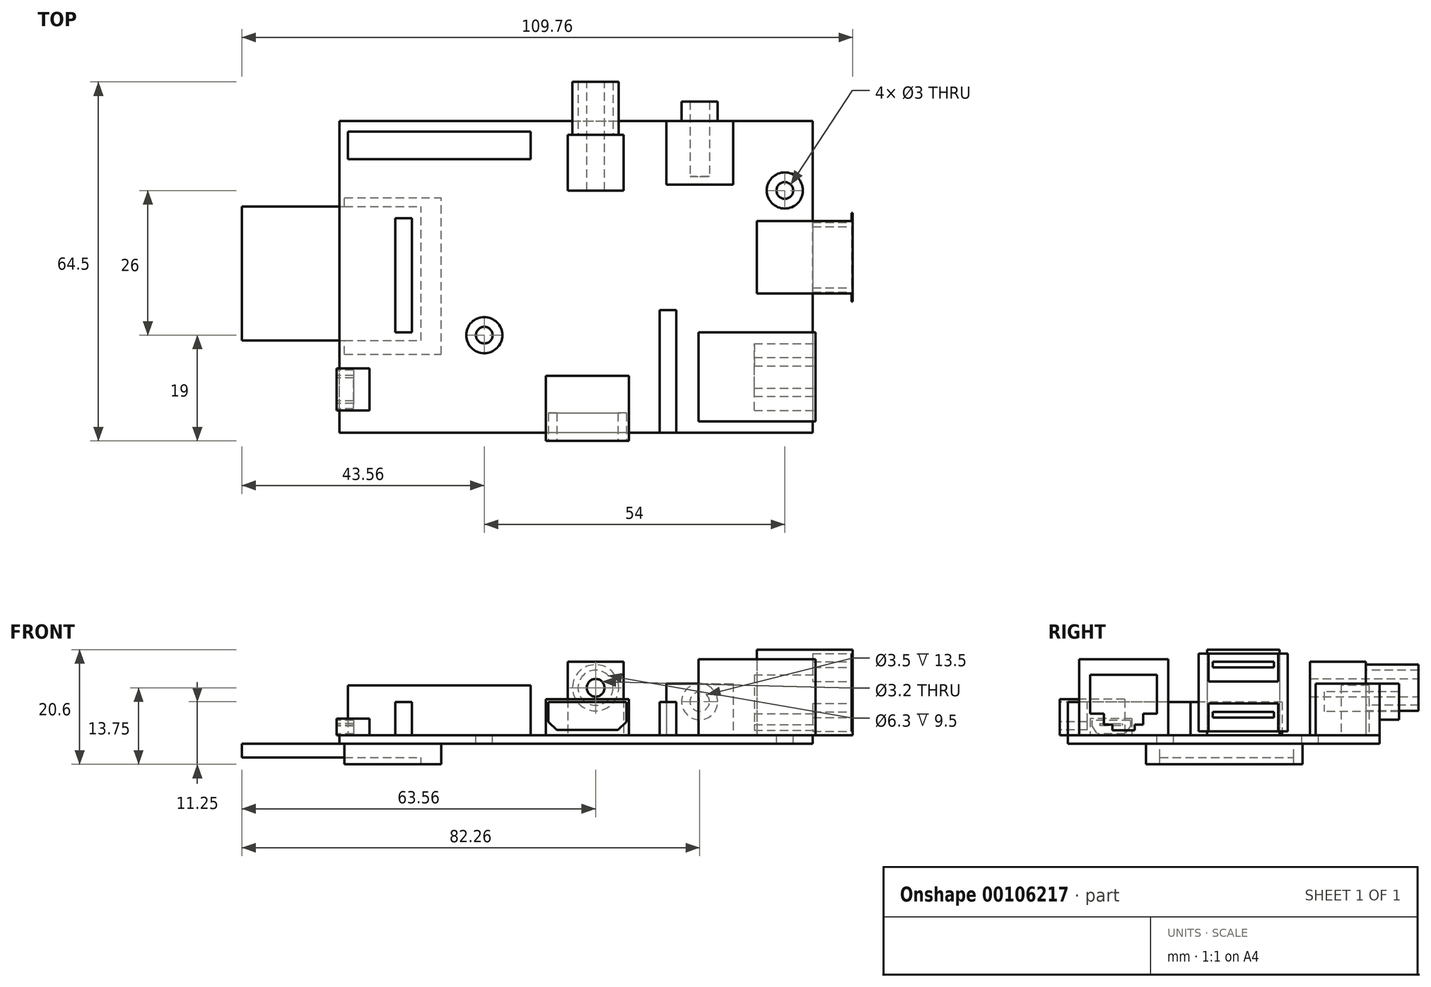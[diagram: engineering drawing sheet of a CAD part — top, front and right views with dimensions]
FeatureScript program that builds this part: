
annotation { "Feature Type Name" : "Feature", "Feature Type Description" : "" }
export const myFeature = defineFeature(function(context is Context, id is Id, definition is map)
    precondition{}
    {
        {
            var Q0;
            Q0=qCreatedBy(makeId("Top.planeOp"),FACE);
            var sketch = newSketch(context, id + "F0", { "sketchPlane" : qUnion([Q0])});
            skLineSegment(sketch, "E0", {"start": v(-47.7, 28) * mm, "end": v(37.3, 28) * mm});
            skLineSegment(sketch, "E1", {"start": v(37.3, 28) * mm, "end": v(37.3, -28) * mm});
            skLineSegment(sketch, "E2", {"start": v(37.3, -28) * mm, "end": v(-47.7, -28) * mm});
            skLineSegment(sketch, "E3", {"start": v(-47.7, -28) * mm, "end": v(-47.7, 28) * mm});
            skCircle(sketch, "E4", {"center": v(32.3, 15.5) * mm, "radius": 3.25 * mm});
            skCircle(sketch, "E5", {"center": v(-21.7, -10.5) * mm, "radius": 3.25 * mm});
            skLineSegment(sketch, "E6.bottom", {"start": v(37.8, -10) * mm, "end": v(16.8, -10) * mm});
            skLineSegment(sketch, "E6.top", {"start": v(37.8, -26) * mm, "end": v(16.8, -26) * mm});
            skLineSegment(sketch, "E6.left", {"start": v(37.8, -10) * mm, "end": v(37.8, -26) * mm});
            skLineSegment(sketch, "E6.right", {"start": v(16.8, -10) * mm, "end": v(16.8, -26) * mm});
            skLineSegment(sketch, "E7.bottom", {"start": v(27.3, 10) * mm, "end": v(44.3, 10) * mm});
            skLineSegment(sketch, "E7.top", {"start": v(27.3, -3) * mm, "end": v(44.3, -3) * mm});
            skLineSegment(sketch, "E7.left", {"start": v(27.3, 10) * mm, "end": v(27.3, -3) * mm});
            skLineSegment(sketch, "E7.right", {"start": v(44.3, 10) * mm, "end": v(44.3, -3) * mm});
            skLineSegment(sketch, "E8", {"start": v(0, 28) * mm, "end": v(0, -28) * mm, "construction": true});
            skLineSegment(sketch, "E9", {"start": v(-47.7, 0) * mm, "end": v(37.3, 0) * mm, "construction": true});
            skPoint(sketch, "E10", {"position": v(0, 0) * mm});
            skLineSegment(sketch, "E11.bottom", {"start": v(-10.64, -17.8) * mm, "end": v(4.3, -17.8) * mm});
            skLineSegment(sketch, "E11.top", {"start": v(-10.64, -29.5) * mm, "end": v(4.3, -29.5) * mm});
            skLineSegment(sketch, "E11.left", {"start": v(-10.64, -17.8) * mm, "end": v(-10.64, -29.5) * mm});
            skLineSegment(sketch, "E11.right", {"start": v(4.3, -17.8) * mm, "end": v(4.3, -29.5) * mm});
            skLineSegment(sketch, "E12.bottom", {"start": v(11, 28.03) * mm, "end": v(23, 28.03) * mm});
            skLineSegment(sketch, "E12.top", {"start": v(11, 16.53) * mm, "end": v(23, 16.53) * mm});
            skLineSegment(sketch, "E12.left", {"start": v(11, 28.03) * mm, "end": v(11, 16.53) * mm});
            skLineSegment(sketch, "E12.right", {"start": v(23, 28.03) * mm, "end": v(23, 16.53) * mm});
            skLineSegment(sketch, "E13.bottom", {"start": v(-6.7, 25.5) * mm, "end": v(3.3, 25.5) * mm});
            skLineSegment(sketch, "E13.top", {"start": v(-6.7, 15.5) * mm, "end": v(3.3, 15.5) * mm});
            skLineSegment(sketch, "E13.left", {"start": v(-6.7, 25.5) * mm, "end": v(-6.7, 15.5) * mm});
            skLineSegment(sketch, "E13.right", {"start": v(3.3, 25.5) * mm, "end": v(3.3, 15.5) * mm});
            skLineSegment(sketch, "E14.bottom", {"start": v(-46.2, 26.1) * mm, "end": v(-13.4, 26.1) * mm});
            skLineSegment(sketch, "E14.top", {"start": v(-46.2, 21.1) * mm, "end": v(-13.4, 21.1) * mm});
            skLineSegment(sketch, "E14.left", {"start": v(-46.2, 26.1) * mm, "end": v(-46.2, 21.1) * mm});
            skLineSegment(sketch, "E14.right", {"start": v(-13.4, 26.1) * mm, "end": v(-13.4, 21.1) * mm});
            skLineSegment(sketch, "E15.bottom", {"start": v(-46.7, 14.11) * mm, "end": v(-29.7, 14.11) * mm});
            skLineSegment(sketch, "E15.top", {"start": v(-46.7, -13.89) * mm, "end": v(-29.7, -13.89) * mm});
            skLineSegment(sketch, "E15.left", {"start": v(-46.7, 14.11) * mm, "end": v(-46.7, -13.89) * mm});
            skLineSegment(sketch, "E15.right", {"start": v(-29.7, 14.11) * mm, "end": v(-29.7, -13.89) * mm});
            skLineSegment(sketch, "E16.bottom", {"start": v(-65.2, 12.61) * mm, "end": v(-33.2, 12.61) * mm});
            skLineSegment(sketch, "E16.top", {"start": v(-65.2, -11.39) * mm, "end": v(-33.2, -11.39) * mm});
            skLineSegment(sketch, "E16.left", {"start": v(-65.2, 12.61) * mm, "end": v(-65.2, -11.39) * mm});
            skLineSegment(sketch, "E16.right", {"start": v(-33.2, 12.61) * mm, "end": v(-33.2, -11.39) * mm});
            skLineSegment(sketch, "E17.bottom", {"start": v(-48.2, -16.5) * mm, "end": v(-42.3, -16.5) * mm});
            skLineSegment(sketch, "E17.top", {"start": v(-48.2, -24) * mm, "end": v(-42.3, -24) * mm});
            skLineSegment(sketch, "E17.left", {"start": v(-48.2, -16.5) * mm, "end": v(-48.2, -24) * mm});
            skLineSegment(sketch, "E17.right", {"start": v(-42.3, -16.5) * mm, "end": v(-42.3, -24) * mm});
            skLineSegment(sketch, "E18.bottom", {"start": v(9.8, -6) * mm, "end": v(12.8, -6) * mm});
            skLineSegment(sketch, "E18.top", {"start": v(9.8, -28) * mm, "end": v(12.8, -28) * mm});
            skLineSegment(sketch, "E18.left", {"start": v(9.8, -6) * mm, "end": v(9.8, -28) * mm});
            skLineSegment(sketch, "E18.right", {"start": v(12.8, -6) * mm, "end": v(12.8, -28) * mm});
            skCircle(sketch, "E19", {"center": v(32.3, 15.5) * mm, "radius": 1.5 * mm});
            skCircle(sketch, "E20", {"center": v(-21.7, -10.5) * mm, "radius": 1.5 * mm});
            skLineSegment(sketch, "E21.bottom", {"start": v(-37.7, 10.5) * mm, "end": v(-34.7, 10.5) * mm});
            skLineSegment(sketch, "E21.top", {"start": v(-37.7, -10) * mm, "end": v(-34.7, -10) * mm});
            skLineSegment(sketch, "E21.left", {"start": v(-37.7, 10.5) * mm, "end": v(-37.7, -10) * mm});
            skLineSegment(sketch, "E21.right", {"start": v(-34.7, 10.5) * mm, "end": v(-34.7, -10) * mm});
            skSolve(sketch);
        }
        {
            var Q0;
            {var subQ9=sQuery(id+"F0.wireOp",EDGE,"E0");Q0=makeQuery(id+"F0.imprint","IMPRINT",FACE,{"disambiguationData":[TD([[makeQuery(id+"F0.imprint","IMPRINT",EDGE,{"derivedFrom":subQ9}),-1.0]])]});}
            var Q1;
            {var subQ5=sQuery(id+"F0.wireOp",EDGE,"E7.left");Q1=makeQuery(id+"F0.imprint","IMPRINT",FACE,{"disambiguationData":[TD([[makeQuery(id+"F0.imprint","IMPRINT",EDGE,{"derivedFrom":subQ5}),1.0]])]});}
            var Q2;
            Q2=makeQuery(id+"F0.imprint","IMPRINT",FACE,{"disambiguationData":[TD([[makeQuery(id+"F0.imprint","IMPRINT",EDGE,{"derivedFrom":sQuery(id+"F0.wireOp",EDGE,"E4")}),1.0]])]});
            var Q3;
            Q3=makeQuery(id+"F0.imprint","IMPRINT",FACE,{"disambiguationData":[TD([[makeQuery(id+"F0.imprint","IMPRINT",EDGE,{"derivedFrom":sQuery(id+"F0.wireOp",EDGE,"E5")}),1.0]])]});
            var Q4;
            {var subQ5=sQuery(id+"F0.wireOp",EDGE,"E6.right");Q4=makeQuery(id+"F0.imprint","IMPRINT",FACE,{"disambiguationData":[TD([[makeQuery(id+"F0.imprint","IMPRINT",EDGE,{"derivedFrom":subQ5}),1.0]])]});}
            var Q5;
            {var subQ5=sQuery(id+"F0.wireOp",EDGE,"E15.bottom");Q5=makeQuery(id+"F0.imprint","IMPRINT",FACE,{"disambiguationData":[TD([[makeQuery(id+"F0.imprint","IMPRINT",EDGE,{"derivedFrom":subQ5}),-1.0]])]});}
            var Q6;
            {var subQ5=sQuery(id+"F0.wireOp",EDGE,"E16.right");Q6=makeQuery(id+"F0.imprint","IMPRINT",FACE,{"disambiguationData":[TD([[makeQuery(id+"F0.imprint","IMPRINT",EDGE,{"derivedFrom":subQ5}),-1.0]])]});}
            var Q7;
            {var subQ0=sQuery(id+"F0.wireOp",EDGE,"E16.top");var subQ1=sQuery(id+"F0.wireOp",EDGE,"E3");var subQ2=makeQuery(id+"F0.imprint","INTERSECT",VERTEX,{"derivedFrom":[subQ1,subQ0]});Q7=makeQuery(id+"F0.imprint","IMPRINT",FACE,{"disambiguationData":[TD([[makeQuery(id+"F0.imprint","IMPRINT",EDGE,{"disambiguationData":[TD([[subQ2,-1.0]])],"derivedFrom":subQ1}),-1.0]])]});}
            var Q8;
            {var subQ5=sQuery(id+"F0.wireOp",EDGE,"E17.right");Q8=makeQuery(id+"F0.imprint","IMPRINT",FACE,{"disambiguationData":[TD([[makeQuery(id+"F0.imprint","IMPRINT",EDGE,{"derivedFrom":subQ5}),-1.0]])]});}
            var Q9;
            Q9=makeQuery(id+"F0.imprint","IMPRINT",FACE,{"disambiguationData":[TD([[makeQuery(id+"F0.imprint","IMPRINT",EDGE,{"derivedFrom":sQuery(id+"F0.wireOp",EDGE,"E14.bottom")}),-1.0]])]});
            var Q10;
            Q10=makeQuery(id+"F0.imprint","IMPRINT",FACE,{"disambiguationData":[TD([[makeQuery(id+"F0.imprint","IMPRINT",EDGE,{"derivedFrom":sQuery(id+"F0.wireOp",EDGE,"E13.bottom")}),-1.0]])]});
            var Q11;
            {var subQ5=sQuery(id+"F0.wireOp",EDGE,"E12.top");Q11=makeQuery(id+"F0.imprint","IMPRINT",FACE,{"disambiguationData":[TD([[makeQuery(id+"F0.imprint","IMPRINT",EDGE,{"derivedFrom":subQ5}),1.0]])]});}
            var Q12;
            {var subQ5=sQuery(id+"F0.wireOp",EDGE,"E11.bottom");Q12=makeQuery(id+"F0.imprint","IMPRINT",FACE,{"disambiguationData":[TD([[makeQuery(id+"F0.imprint","IMPRINT",EDGE,{"derivedFrom":subQ5}),-1.0]])]});}
            var Q13;
            Q13=makeQuery(id+"F0.imprint","IMPRINT",FACE,{"disambiguationData":[TD([[makeQuery(id+"F0.imprint","IMPRINT",EDGE,{"derivedFrom":sQuery(id+"F0.wireOp",EDGE,"E18.bottom")}),-1.0]])]});
            var Q14;
            Q14=makeQuery(id+"F0.imprint","IMPRINT",FACE,{"disambiguationData":[TD([[makeQuery(id+"F0.imprint","IMPRINT",EDGE,{"derivedFrom":sQuery(id+"F0.wireOp",EDGE,"E21.bottom")}),-1.0]])]});
            extrude(context, id + "F1", {"entities" : qUnion([Q0, Q1, Q2, Q3, Q4, Q5, Q6, Q7, Q8, Q9, Q10, Q11, Q12, Q13, Q14]), "oppositeDirection" : true, "depth" : 1.5 * mm});
        }
        {
            var Q0;
            {var subQ5=sQuery(id+"F0.wireOp",EDGE,"E6.right");Q0=makeQuery(id+"F0.imprint","IMPRINT",FACE,{"disambiguationData":[TD([[makeQuery(id+"F0.imprint","IMPRINT",EDGE,{"derivedFrom":subQ5}),1.0]])]});}
            var Q1;
            {var subQ5=sQuery(id+"F0.wireOp",EDGE,"E6.left");Q1=makeQuery(id+"F0.imprint","IMPRINT",FACE,{"disambiguationData":[TD([[makeQuery(id+"F0.imprint","IMPRINT",EDGE,{"derivedFrom":subQ5}),-1.0]])]});}
            extrude(context, id + "F2", {"entities" : qUnion([Q0, Q1]), "depth" : 13.7 * mm});
        }
        {
            var Q0;
            {var subQ5=sQuery(id+"F0.wireOp",EDGE,"E7.left");Q0=makeQuery(id+"F0.imprint","IMPRINT",FACE,{"disambiguationData":[TD([[makeQuery(id+"F0.imprint","IMPRINT",EDGE,{"derivedFrom":subQ5}),1.0]])]});}
            var Q1;
            {var subQ5=sQuery(id+"F0.wireOp",EDGE,"E7.right");Q1=makeQuery(id+"F0.imprint","IMPRINT",FACE,{"disambiguationData":[TD([[makeQuery(id+"F0.imprint","IMPRINT",EDGE,{"derivedFrom":subQ5}),-1.0]])]});}
            extrude(context, id + "F3", {"entities" : qUnion([Q0, Q1]), "depth" : 15.4 * mm});
        }
        {
            var Q0;
            {var subQ5=sQuery(id+"F0.wireOp",EDGE,"E12.top");Q0=makeQuery(id+"F0.imprint","IMPRINT",FACE,{"disambiguationData":[TD([[makeQuery(id+"F0.imprint","IMPRINT",EDGE,{"derivedFrom":subQ5}),1.0]])]});}
            extrude(context, id + "F4", {"entities" : qUnion([Q0]), "depth" : 9.3 * mm});
        }
        {
            var Q0;
            Q0=makeQuery(id+"F0.imprint","IMPRINT",FACE,{"disambiguationData":[TD([[makeQuery(id+"F0.imprint","IMPRINT",EDGE,{"derivedFrom":sQuery(id+"F0.wireOp",EDGE,"E13.bottom")}),-1.0]])]});
            extrude(context, id + "F5", {"entities" : qUnion([Q0]), "depth" : 13.2 * mm});
        }
        {
            var Q0;
            Q0=makeQuery(id+"F0.imprint","IMPRINT",FACE,{"disambiguationData":[TD([[makeQuery(id+"F0.imprint","IMPRINT",EDGE,{"derivedFrom":sQuery(id+"F0.wireOp",EDGE,"E14.bottom")}),-1.0]])]});
            extrude(context, id + "F6", {"entities" : qUnion([Q0]), "depth" : 9 * mm});
        }
        {
            var Q0;
            Q0=makeQuery(id+"F0.imprint","IMPRINT",FACE,{"disambiguationData":[TD([[makeQuery(id+"F0.imprint","IMPRINT",EDGE,{"derivedFrom":sQuery(id+"F0.wireOp",EDGE,"E18.bottom")}),-1.0]])]});
            extrude(context, id + "F7", {"entities" : qUnion([Q0]), "depth" : 6 * mm});
        }
        {
            var Q0;
            {var subQ5=sQuery(id+"F0.wireOp",EDGE,"E11.bottom");Q0=makeQuery(id+"F0.imprint","IMPRINT",FACE,{"disambiguationData":[TD([[makeQuery(id+"F0.imprint","IMPRINT",EDGE,{"derivedFrom":subQ5}),-1.0]])]});}
            var Q1;
            {var subQ5=sQuery(id+"F0.wireOp",EDGE,"E11.top");Q1=makeQuery(id+"F0.imprint","IMPRINT",FACE,{"disambiguationData":[TD([[makeQuery(id+"F0.imprint","IMPRINT",EDGE,{"derivedFrom":subQ5}),1.0]])]});}
            extrude(context, id + "F8", {"entities" : qUnion([Q0, Q1]), "depth" : 6.5 * mm});
        }
        {
            var Q0;
            Q0=makeQuery(id+"F0.imprint","IMPRINT",FACE,{"disambiguationData":[TD([[makeQuery(id+"F0.imprint","IMPRINT",EDGE,{"derivedFrom":sQuery(id+"F0.wireOp",EDGE,"E4")}),1.0]])]});
            var Q1;
            Q1=makeQuery(id+"F0.imprint","IMPRINT",FACE,{"disambiguationData":[TD([[makeQuery(id+"F0.imprint","IMPRINT",EDGE,{"derivedFrom":sQuery(id+"F0.wireOp",EDGE,"E5")}),1.0]])]});
            extrude(context, id + "F9", {"entities" : qUnion([Q0, Q1]), "depth" : 0.01 * mm});
        }
        {
            var Q0;
            {var subQ5=sQuery(id+"F0.wireOp",EDGE,"E17.right");Q0=makeQuery(id+"F0.imprint","IMPRINT",FACE,{"disambiguationData":[TD([[makeQuery(id+"F0.imprint","IMPRINT",EDGE,{"derivedFrom":subQ5}),-1.0]])]});}
            var Q1;
            {var subQ5=sQuery(id+"F0.wireOp",EDGE,"E17.left");Q1=makeQuery(id+"F0.imprint","IMPRINT",FACE,{"disambiguationData":[TD([[makeQuery(id+"F0.imprint","IMPRINT",EDGE,{"derivedFrom":subQ5}),1.0]])]});}
            extrude(context, id + "F10", {"entities" : qUnion([Q0, Q1]), "depth" : 3 * mm});
        }
        {
            var Q0;
            Q0=makeQuery(id+"F0.imprint","IMPRINT",FACE,{"disambiguationData":[TD([[makeQuery(id+"F0.imprint","IMPRINT",EDGE,{"derivedFrom":sQuery(id+"F0.wireOp",EDGE,"E21.bottom")}),-1.0]])]});
            extrude(context, id + "F11", {"entities" : qUnion([Q0]), "depth" : 6 * mm});
        }
        {
            var Q0;
            Q0=makeQuery(id+"F1.opExtrude","CAP_FACE",FACE,{"disambiguationData":[OSD([sQuery(id+"F0.wireOp",EDGE,"E0"),sQuery(id+"F0.wireOp",EDGE,"E1"),sQuery(id+"F0.wireOp",EDGE,"E2"),sQuery(id+"F0.wireOp",EDGE,"E3"),sQuery(id+"F0.wireOp",EDGE,"E18.top"),sQuery(id+"F0.wireOp",EDGE,"E19"),sQuery(id+"F0.wireOp",EDGE,"E20")])],"isStart":false});
            var sketch = newSketch(context, id + "F12", { "sketchPlane" : qUnion([Q0])});
            skLineSegment(sketch, "E22.bottom", {"start": v(-65.26, 11.49) * mm, "end": v(-33.09, 11.49) * mm});
            skLineSegment(sketch, "E22.top", {"start": v(-65.26, -12.6) * mm, "end": v(-33.09, -12.6) * mm});
            skLineSegment(sketch, "E22.left", {"start": v(-65.26, 11.49) * mm, "end": v(-65.26, -12.6) * mm});
            skLineSegment(sketch, "E22.right", {"start": v(-33.09, 11.49) * mm, "end": v(-33.09, -12.6) * mm});
            skLineSegment(sketch, "E23.bottom", {"start": v(-46.8, 13.96) * mm, "end": v(-29.45, 13.96) * mm});
            skLineSegment(sketch, "E23.top", {"start": v(-46.8, -14.17) * mm, "end": v(-29.45, -14.17) * mm});
            skLineSegment(sketch, "E23.left", {"start": v(-46.8, 13.96) * mm, "end": v(-46.8, -14.17) * mm});
            skLineSegment(sketch, "E23.right", {"start": v(-29.45, 13.96) * mm, "end": v(-29.45, -14.17) * mm});
            skSolve(sketch);
        }
        {
            var Q0;
            {var subQ1=sQuery(id+"F12.wireOp",EDGE,"E22.right");Q0=makeQuery(id+"F12.imprint","IMPRINT",FACE,{"disambiguationData":[TD([[makeQuery(id+"F12.imprint","IMPRINT",EDGE,{"derivedFrom":subQ1}),1.0]])]});}
            extrude(context, id + "F13", {"entities" : qUnion([Q0]), "depth" : 3.7 * mm});
        }
        {
            var Q0;
            {var subQ0=sQuery(id+"F12.wireOp",EDGE,"E22.right");Q0=makeQuery(id+"F12.imprint","IMPRINT",FACE,{"disambiguationData":[TD([[makeQuery(id+"F12.imprint","IMPRINT",EDGE,{"derivedFrom":subQ0}),-1.0]])]});}
            var Q1;
            {var subQ0=sQuery(id+"F12.wireOp",EDGE,"E23.left");var subQ1=sQuery(id+"F12.wireOp",EDGE,"E22.bottom");var subQ2=makeQuery(id+"F12.imprint","INTERSECT",VERTEX,{"derivedFrom":[subQ1,subQ0]});Q1=makeQuery(id+"F12.imprint","IMPRINT",FACE,{"disambiguationData":[TD([[makeQuery(id+"F12.imprint","IMPRINT",EDGE,{"disambiguationData":[TD([[subQ2,1.0]])],"derivedFrom":subQ1}),-1.0]])]});}
            var Q2;
            {var subQ0=sQuery(id+"F12.wireOp",EDGE,"E22.left");Q2=makeQuery(id+"F12.imprint","IMPRINT",FACE,{"disambiguationData":[TD([[makeQuery(id+"F12.imprint","IMPRINT",EDGE,{"derivedFrom":subQ0}),1.0]])]});}
            extrude(context, id + "F14", {"entities" : qUnion([Q0, Q1, Q2]), "operationType" : NewBodyOperationType.ADD, "depth" : 2.5 * mm});
        }
        {
            var Q0;
            Q0=makeQuery(id+"F4.opExtrude","SWEPT_FACE",FACE,{"disambiguationData":[OSD([sQuery(id+"F0.wireOp",EDGE,"E0")])]});
            var sketch = newSketch(context, id + "F15", { "sketchPlane" : qUnion([Q0])});
            skLineSegment(sketch, "E24", {"start": v(-17, 9.3) * mm, "end": v(-17, 0) * mm, "construction": true});
            skCircle(sketch, "E25", {"center": v(-17, 6.05) * mm, "radius": 3.25 * mm});
            skCircle(sketch, "E26", {"center": v(-17, 6.05) * mm, "radius": 1.75 * mm});
            skSolve(sketch);
        }
        {
            var Q0;
            Q0=makeQuery(id+"F15.imprint","IMPRINT",FACE,{"disambiguationData":[TD([[makeQuery(id+"F15.imprint","IMPRINT",EDGE,{"derivedFrom":sQuery(id+"F15.wireOp",EDGE,"E25")}),1.0]])]});
            extrude(context, id + "F16", {"entities" : qUnion([Q0]), "operationType" : NewBodyOperationType.ADD, "depth" : 3.5 * mm});
        }
        {
            var Q0;
            Q0=makeQuery(id+"F15.imprint","IMPRINT",FACE,{"disambiguationData":[TD([[makeQuery(id+"F15.imprint","IMPRINT",EDGE,{"derivedFrom":sQuery(id+"F15.wireOp",EDGE,"E26")}),1.0]])]});
            var Q1;
            Q1=sQuery(id+"F15.wireOp",EDGE,"E26");
            extrude(context, id + "F17", {"entities" : qUnion([Q0]), "operationType" : NewBodyOperationType.REMOVE, "surfaceEntities" : qUnion([Q1]), "oppositeDirection" : true, "depth" : 10 * mm});
        }
        {
            var Q0;
            Q0=makeQuery(id+"F5.opExtrude","SWEPT_FACE",FACE,{"disambiguationData":[OSD([sQuery(id+"F0.wireOp",EDGE,"E13.bottom")])]});
            var sketch = newSketch(context, id + "F18", { "sketchPlane" : qUnion([Q0])});
            skLineSegment(sketch, "E27", {"start": v(1.7, 13.2) * mm, "end": v(1.7, 0) * mm, "construction": true});
            skLineSegment(sketch, "E28", {"start": v(-3.3, 12.7) * mm, "end": v(6.7, 12.7) * mm, "construction": true});
            skCircle(sketch, "E29", {"center": v(1.7, 8.55) * mm, "radius": 4.15 * mm});
            skCircle(sketch, "E30", {"center": v(1.7, 8.55) * mm, "radius": 3.15 * mm});
            skCircle(sketch, "E31", {"center": v(1.7, 8.55) * mm, "radius": 1.6 * mm});
            skSolve(sketch);
        }
        {
            var Q0;
            Q0=makeQuery(id+"F18.imprint","IMPRINT",FACE,{"disambiguationData":[TD([[makeQuery(id+"F18.imprint","IMPRINT",EDGE,{"derivedFrom":sQuery(id+"F18.wireOp",EDGE,"E31")}),1.0]])]});
            extrude(context, id + "F19", {"entities" : qUnion([Q0]), "operationType" : NewBodyOperationType.REMOVE, "endBound" : BoundingType.THROUGH_ALL, "oppositeDirection" : true, "depth" : 25 * mm});
        }
        {
            var Q0;
            Q0=makeQuery(id+"F18.imprint","IMPRINT",FACE,{"disambiguationData":[TD([[makeQuery(id+"F18.imprint","IMPRINT",EDGE,{"derivedFrom":sQuery(id+"F18.wireOp",EDGE,"E30")}),1.0]])]});
            extrude(context, id + "F20", {"entities" : qUnion([Q0]), "operationType" : NewBodyOperationType.ADD, "depth" : 9.5 * mm});
        }
        {
            var Q0;
            Q0=makeQuery(id+"F18.imprint","IMPRINT",FACE,{"disambiguationData":[TD([[makeQuery(id+"F18.imprint","IMPRINT",EDGE,{"derivedFrom":sQuery(id+"F18.wireOp",EDGE,"E29")}),1.0]])]});
            extrude(context, id + "F21", {"entities" : qUnion([Q0]), "depth" : 9.5 * mm});
        }
        {
            var Q0;
            Q0=makeQuery(id+"F8.opExtrude","SWEPT_FACE",FACE,{"disambiguationData":[OSD([sQuery(id+"F0.wireOp",EDGE,"E11.top")])]});
            var sketch = newSketch(context, id + "F22", { "sketchPlane" : qUnion([Q0])});
            skLineSegment(sketch, "E32", {"start": v(-10.64, 3.25) * mm, "end": v(4.3, 3.25) * mm, "construction": true});
            skLineSegment(sketch, "E33", {"start": v(-3.17, 6.5) * mm, "end": v(-3.17, 0) * mm, "construction": true});
            skLineSegment(sketch, "E34", {"start": v(3.83, 6) * mm, "end": v(3.83, 2.43) * mm});
            skLineSegment(sketch, "E35", {"start": v(3.83, 2.43) * mm, "end": v(2.33, 1) * mm});
            skLineSegment(sketch, "E36", {"start": v(-8.67, 1) * mm, "end": v(-10.17, 2.43) * mm});
            skLineSegment(sketch, "E37", {"start": v(-10.17, 2.43) * mm, "end": v(-10.17, 6) * mm});
            skLineSegment(sketch, "E38", {"start": v(-10.17, 6) * mm, "end": v(-3.17, 6) * mm});
            skLineSegment(sketch, "E39", {"start": v(-3.17, 6) * mm, "end": v(3.83, 6) * mm});
            skLineSegment(sketch, "E40", {"start": v(-8.67, 1) * mm, "end": v(-3.17, 1) * mm});
            skLineSegment(sketch, "E41", {"start": v(-3.17, 1) * mm, "end": v(2.33, 1) * mm});
            skSolve(sketch);
        }
        {
            var Q0;
            Q0=makeQuery(id+"F22.imprint","IMPRINT",FACE,{"disambiguationData":[TD([[makeQuery(id+"F22.imprint","IMPRINT",EDGE,{"derivedFrom":sQuery(id+"F22.wireOp",EDGE,"E34")}),-1.0]])]});
            extrude(context, id + "F23", {"entities" : qUnion([Q0]), "operationType" : NewBodyOperationType.REMOVE, "oppositeDirection" : true, "depth" : 5 * mm});
        }
        {
            var Q0;
            Q0=makeQuery(id+"F2.opExtrude","SWEPT_FACE",FACE,{"disambiguationData":[OSD([sQuery(id+"F0.wireOp",EDGE,"E6.left")])]});
            var sketch = newSketch(context, id + "F24", { "sketchPlane" : qUnion([Q0])});
            skLineSegment(sketch, "E42", {"start": v(-18, 13.7) * mm, "end": v(-18, 0) * mm, "construction": true});
            skLineSegment(sketch, "E43", {"start": v(-18, 10.9) * mm, "end": v(-12, 10.9) * mm});
            skLineSegment(sketch, "E44", {"start": v(-12, 10.9) * mm, "end": v(-12, 3.9) * mm});
            skLineSegment(sketch, "E45", {"start": v(-12, 3.9) * mm, "end": v(-14.5, 3.9) * mm});
            skLineSegment(sketch, "E46", {"start": v(-14.5, 3.9) * mm, "end": v(-14.5, 1.9) * mm});
            skLineSegment(sketch, "E47", {"start": v(-14.5, 1.9) * mm, "end": v(-16, 1.9) * mm});
            skLineSegment(sketch, "E48", {"start": v(-16, 1.9) * mm, "end": v(-16, 0.9) * mm});
            skLineSegment(sketch, "E49", {"start": v(-16, 0.9) * mm, "end": v(-18, 0.9) * mm});
            skLineSegment(sketch, "E50.MirrorCS", {"start": v(-18, 10.9) * mm, "end": v(-24, 10.9) * mm});
            skLineSegment(sketch, "E51.MirrorCS", {"start": v(-24, 10.9) * mm, "end": v(-24, 3.9) * mm});
            skLineSegment(sketch, "E52.MirrorCS", {"start": v(-24, 3.9) * mm, "end": v(-21.5, 3.9) * mm});
            skLineSegment(sketch, "E53.MirrorCS", {"start": v(-21.5, 3.9) * mm, "end": v(-21.5, 1.9) * mm});
            skLineSegment(sketch, "E54.MirrorCS", {"start": v(-21.5, 1.9) * mm, "end": v(-20, 1.9) * mm});
            skLineSegment(sketch, "E55.MirrorCS", {"start": v(-20, 1.9) * mm, "end": v(-20, 0.9) * mm});
            skLineSegment(sketch, "E56.MirrorCS", {"start": v(-20, 0.9) * mm, "end": v(-18, 0.9) * mm});
            skSolve(sketch);
        }
        {
            var Q0;
            Q0=makeQuery(id+"F24.imprint","IMPRINT",FACE,{"disambiguationData":[TD([[makeQuery(id+"F24.imprint","IMPRINT",EDGE,{"derivedFrom":sQuery(id+"F24.wireOp",EDGE,"E43")}),-1.0]])]});
            extrude(context, id + "F25", {"entities" : qUnion([Q0]), "operationType" : NewBodyOperationType.REMOVE, "oppositeDirection" : true, "depth" : 11 * mm});
        }
        {
            var Q0;
            Q0=makeQuery(id+"F3.opExtrude","SWEPT_FACE",FACE,{"disambiguationData":[OSD([sQuery(id+"F0.wireOp",EDGE,"E7.right")])]});
            var sketch = newSketch(context, id + "F26", { "sketchPlane" : qUnion([Q0])});
            skLineSegment(sketch, "E57", {"start": v(3.5, 15.4) * mm, "end": v(3.5, 0) * mm, "construction": true});
            skLineSegment(sketch, "E58", {"start": v(3.5, 14.7) * mm, "end": v(9.75, 14.7) * mm});
            skLineSegment(sketch, "E59", {"start": v(9.75, 14.7) * mm, "end": v(9.75, 9.7) * mm});
            skLineSegment(sketch, "E60", {"start": v(9.75, 9.7) * mm, "end": v(3.5, 9.7) * mm});
            skLineSegment(sketch, "E61", {"start": v(3.5, 5.7) * mm, "end": v(9.75, 5.7) * mm});
            skLineSegment(sketch, "E62", {"start": v(9.75, 5.7) * mm, "end": v(9.75, 0.7) * mm});
            skLineSegment(sketch, "E63", {"start": v(9.75, 0.7) * mm, "end": v(3.5, 0.7) * mm});
            skLineSegment(sketch, "E64", {"start": v(3.5, 13.2) * mm, "end": v(9, 13.2) * mm});
            skLineSegment(sketch, "E65", {"start": v(9, 13.2) * mm, "end": v(9, 12.2) * mm});
            skLineSegment(sketch, "E66", {"start": v(9, 12.2) * mm, "end": v(3.5, 12.2) * mm});
            skLineSegment(sketch, "E67", {"start": v(3.5, 4.2) * mm, "end": v(9, 4.2) * mm});
            skLineSegment(sketch, "E68", {"start": v(9, 4.2) * mm, "end": v(9, 3.2) * mm});
            skLineSegment(sketch, "E69", {"start": v(9, 3.2) * mm, "end": v(3.5, 3.2) * mm});
            skLineSegment(sketch, "E70", {"start": v(-3, 7.7) * mm, "end": v(3.5, 7.7) * mm, "construction": true});
            skLineSegment(sketch, "E71", {"start": v(3.5, 7.7) * mm, "end": v(10, 7.7) * mm, "construction": true});
            skLineSegment(sketch, "E72.MirrorCS", {"start": v(3.5, 14.7) * mm, "end": v(-2.75, 14.7) * mm});
            skLineSegment(sketch, "E73.MirrorCS", {"start": v(-2.75, 14.7) * mm, "end": v(-2.75, 9.7) * mm});
            skLineSegment(sketch, "E74.MirrorCS", {"start": v(3.5, 13.2) * mm, "end": v(-2, 13.2) * mm});
            skLineSegment(sketch, "E75.MirrorCS", {"start": v(-2, 13.2) * mm, "end": v(-2, 12.2) * mm});
            skLineSegment(sketch, "E76.MirrorCS", {"start": v(-2, 12.2) * mm, "end": v(3.5, 12.2) * mm});
            skLineSegment(sketch, "E77.MirrorCS", {"start": v(-2.75, 9.7) * mm, "end": v(3.5, 9.7) * mm});
            skLineSegment(sketch, "E78.MirrorCS", {"start": v(3.5, 5.7) * mm, "end": v(-2.75, 5.7) * mm});
            skLineSegment(sketch, "E79.MirrorCS", {"start": v(3.5, 4.2) * mm, "end": v(-2, 4.2) * mm});
            skLineSegment(sketch, "E80.MirrorCS", {"start": v(-2, 3.2) * mm, "end": v(3.5, 3.2) * mm});
            skLineSegment(sketch, "E81.MirrorCS", {"start": v(-2, 4.2) * mm, "end": v(-2, 3.2) * mm});
            skLineSegment(sketch, "E82.MirrorCS", {"start": v(-2.75, 5.7) * mm, "end": v(-2.75, 0.7) * mm});
            skLineSegment(sketch, "E83.MirrorCS", {"start": v(-2.75, 0.7) * mm, "end": v(3.5, 0.7) * mm});
            skSolve(sketch);
        }
        {
            var Q0;
            Q0=makeQuery(id+"F26.imprint","IMPRINT",FACE,{"disambiguationData":[TD([[makeQuery(id+"F26.imprint","IMPRINT",EDGE,{"derivedFrom":sQuery(id+"F26.wireOp",EDGE,"E58")}),-1.0]])]});
            var Q1;
            Q1=makeQuery(id+"F26.imprint","IMPRINT",FACE,{"disambiguationData":[TD([[makeQuery(id+"F26.imprint","IMPRINT",EDGE,{"derivedFrom":sQuery(id+"F26.wireOp",EDGE,"E61")}),-1.0]])]});
            extrude(context, id + "F27", {"entities" : qUnion([Q0, Q1]), "operationType" : NewBodyOperationType.REMOVE, "oppositeDirection" : true, "depth" : 7 * mm});
        }
        {
            var Q0;
            Q0=makeQuery(id+"F10.opExtrude","SWEPT_FACE",FACE,{"disambiguationData":[OSD([sQuery(id+"F0.wireOp",EDGE,"E17.left")])]});
            var sketch = newSketch(context, id + "F28", { "sketchPlane" : qUnion([Q0])});
            skLineSegment(sketch, "E84", {"start": v(20.25, 3) * mm, "end": v(20.25, 0) * mm, "construction": true});
            skLineSegment(sketch, "E85", {"start": v(20.25, 2.7) * mm, "end": v(23.7, 2.7) * mm});
            skLineSegment(sketch, "E86", {"start": v(23.7, 2.7) * mm, "end": v(23.7, 1.66) * mm});
            skLineSegment(sketch, "E87", {"start": v(23.7, 1.66) * mm, "end": v(22.75, 0.3) * mm});
            skLineSegment(sketch, "E88", {"start": v(22.75, 0.3) * mm, "end": v(20.25, 0.3) * mm});
            skLineSegment(sketch, "E89", {"start": v(20.25, 2.1) * mm, "end": v(22.3, 2.1) * mm});
            skLineSegment(sketch, "E90", {"start": v(22.3, 2.1) * mm, "end": v(22.3, 1.8) * mm});
            skLineSegment(sketch, "E91", {"start": v(22.3, 1.8) * mm, "end": v(20.25, 1.8) * mm});
            skLineSegment(sketch, "E92.MirrorCS", {"start": v(20.25, 2.7) * mm, "end": v(16.8, 2.7) * mm});
            skLineSegment(sketch, "E93.MirrorCS", {"start": v(20.25, 2.1) * mm, "end": v(18.2, 2.1) * mm});
            skLineSegment(sketch, "E94.MirrorCS", {"start": v(18.2, 1.8) * mm, "end": v(20.25, 1.8) * mm});
            skLineSegment(sketch, "E95.MirrorCS", {"start": v(18.2, 2.1) * mm, "end": v(18.2, 1.8) * mm});
            skLineSegment(sketch, "E96.MirrorCS", {"start": v(16.8, 2.7) * mm, "end": v(16.8, 1.66) * mm});
            skLineSegment(sketch, "E97.MirrorCS", {"start": v(16.8, 1.66) * mm, "end": v(17.75, 0.3) * mm});
            skLineSegment(sketch, "E98.MirrorCS", {"start": v(17.75, 0.3) * mm, "end": v(20.25, 0.3) * mm});
            skSolve(sketch);
        }
        {
            var Q0;
            Q0=makeQuery(id+"F28.imprint","IMPRINT",FACE,{"disambiguationData":[TD([[makeQuery(id+"F28.imprint","IMPRINT",EDGE,{"derivedFrom":sQuery(id+"F28.wireOp",EDGE,"E85")}),-1.0]])]});
            extrude(context, id + "F29", {"entities" : qUnion([Q0]), "operationType" : NewBodyOperationType.REMOVE, "oppositeDirection" : true, "depth" : 3 * mm});
        }
        {
            var Q0;
            Q0=makeQuery(id+"F26.imprint","IMPRINT",FACE,{"disambiguationData":[TD([[makeQuery(id+"F26.imprint","IMPRINT",EDGE,{"derivedFrom":sQuery(id+"F26.wireOp",EDGE,"E58")}),1.0]])]});
            var sketch = newSketch(context, id + "F30", { "sketchPlane" : qUnion([Q0])});
            skLineSegment(sketch, "E99.0", {"start": v(3.5, 14.7) * mm, "end": v(-2.75, 14.7) * mm});
            skLineSegment(sketch, "E99.1", {"start": v(3.5, 14.7) * mm, "end": v(9.75, 14.7) * mm});
            skLineSegment(sketch, "E99.2", {"start": v(9.75, 14.7) * mm, "end": v(9.75, 9.7) * mm});
            skLineSegment(sketch, "E99.3", {"start": v(9.75, 9.7) * mm, "end": v(3.5, 9.7) * mm});
            skLineSegment(sketch, "E99.4", {"start": v(-2.75, 9.7) * mm, "end": v(3.5, 9.7) * mm});
            skLineSegment(sketch, "E99.5", {"start": v(-2.75, 14.7) * mm, "end": v(-2.75, 9.7) * mm});
            skLineSegment(sketch, "E100.0", {"start": v(10, 15.4) * mm, "end": v(-3, 15.4) * mm});
            skLineSegment(sketch, "E100.1", {"start": v(10, 15.4) * mm, "end": v(10, 0) * mm});
            skLineSegment(sketch, "E100.2", {"start": v(-3, 15.4) * mm, "end": v(-3, 0) * mm});
            skLineSegment(sketch, "E100.3", {"start": v(10, 0) * mm, "end": v(-3, 0) * mm});
            skLineSegment(sketch, "E101.0", {"start": v(3.5, 5.7) * mm, "end": v(-2.75, 5.7) * mm});
            skLineSegment(sketch, "E101.1", {"start": v(3.5, 5.7) * mm, "end": v(9.75, 5.7) * mm});
            skLineSegment(sketch, "E101.2", {"start": v(9.75, 5.7) * mm, "end": v(9.75, 0.7) * mm});
            skLineSegment(sketch, "E101.3", {"start": v(9.75, 0.7) * mm, "end": v(3.5, 0.7) * mm});
            skLineSegment(sketch, "E101.4", {"start": v(-2.75, 0.7) * mm, "end": v(3.5, 0.7) * mm});
            skLineSegment(sketch, "E101.5", {"start": v(-2.75, 5.7) * mm, "end": v(-2.75, 0.7) * mm});
            skLineSegment(sketch, "E102", {"start": v(-3, 15.4) * mm, "end": v(-3, 14.7) * mm});
            skLineSegment(sketch, "E103", {"start": v(-3, 14.7) * mm, "end": v(-4.5, 14.7) * mm});
            skLineSegment(sketch, "E104", {"start": v(-4.5, 14.7) * mm, "end": v(-4.5, 0.7) * mm});
            skLineSegment(sketch, "E105", {"start": v(-4.5, 0.7) * mm, "end": v(-3, 0.7) * mm});
            skLineSegment(sketch, "E106", {"start": v(-3, 0.7) * mm, "end": v(-3, 0) * mm});
            skLineSegment(sketch, "E107", {"start": v(10, 0) * mm, "end": v(10, 0.7) * mm});
            skLineSegment(sketch, "E108", {"start": v(10, 0.7) * mm, "end": v(11.5, 0.7) * mm});
            skLineSegment(sketch, "E109", {"start": v(11.5, 0.7) * mm, "end": v(11.5, 14.7) * mm});
            skLineSegment(sketch, "E110", {"start": v(11.5, 14.7) * mm, "end": v(10, 14.7) * mm});
            skLineSegment(sketch, "E111", {"start": v(10, 14.7) * mm, "end": v(10, 15.4) * mm});
            skLineSegment(sketch, "E112", {"start": v(-4.56, 14.7) * mm, "end": v(3.5, 14.7) * mm, "construction": true});
            skLineSegment(sketch, "E113", {"start": v(3.5, 14.7) * mm, "end": v(11.5, 14.7) * mm, "construction": true});
            skLineSegment(sketch, "E114", {"start": v(-4.5, 0.7) * mm, "end": v(3.5, 0.7) * mm, "construction": true});
            skLineSegment(sketch, "E115", {"start": v(3.5, 0.7) * mm, "end": v(11.5, 0.7) * mm, "construction": true});
            skSolve(sketch);
        }
        {
            var Q0;
            Q0=makeQuery(id+"F30.imprint","IMPRINT",FACE,{"disambiguationData":[TD([[makeQuery(id+"F30.imprint","IMPRINT",EDGE,{"derivedFrom":sQuery(id+"F30.wireOp",EDGE,"E100.2")}),-1.0]])]});
            var Q1;
            Q1=makeQuery(id+"F26.imprint","IMPRINT",FACE,{"disambiguationData":[TD([[makeQuery(id+"F26.imprint","IMPRINT",EDGE,{"derivedFrom":sQuery(id+"F26.wireOp",EDGE,"E58")}),1.0]])]});
            var Q2;
            Q2=makeQuery(id+"F30.imprint","IMPRINT",FACE,{"disambiguationData":[TD([[makeQuery(id+"F30.imprint","IMPRINT",EDGE,{"derivedFrom":sQuery(id+"F30.wireOp",EDGE,"E100.1")}),1.0]])]});
            extrude(context, id + "F31", {"entities" : qUnion([Q0, Q1, Q2]), "operationType" : NewBodyOperationType.ADD, "depth" : 0.2 * mm});
        }
    });
